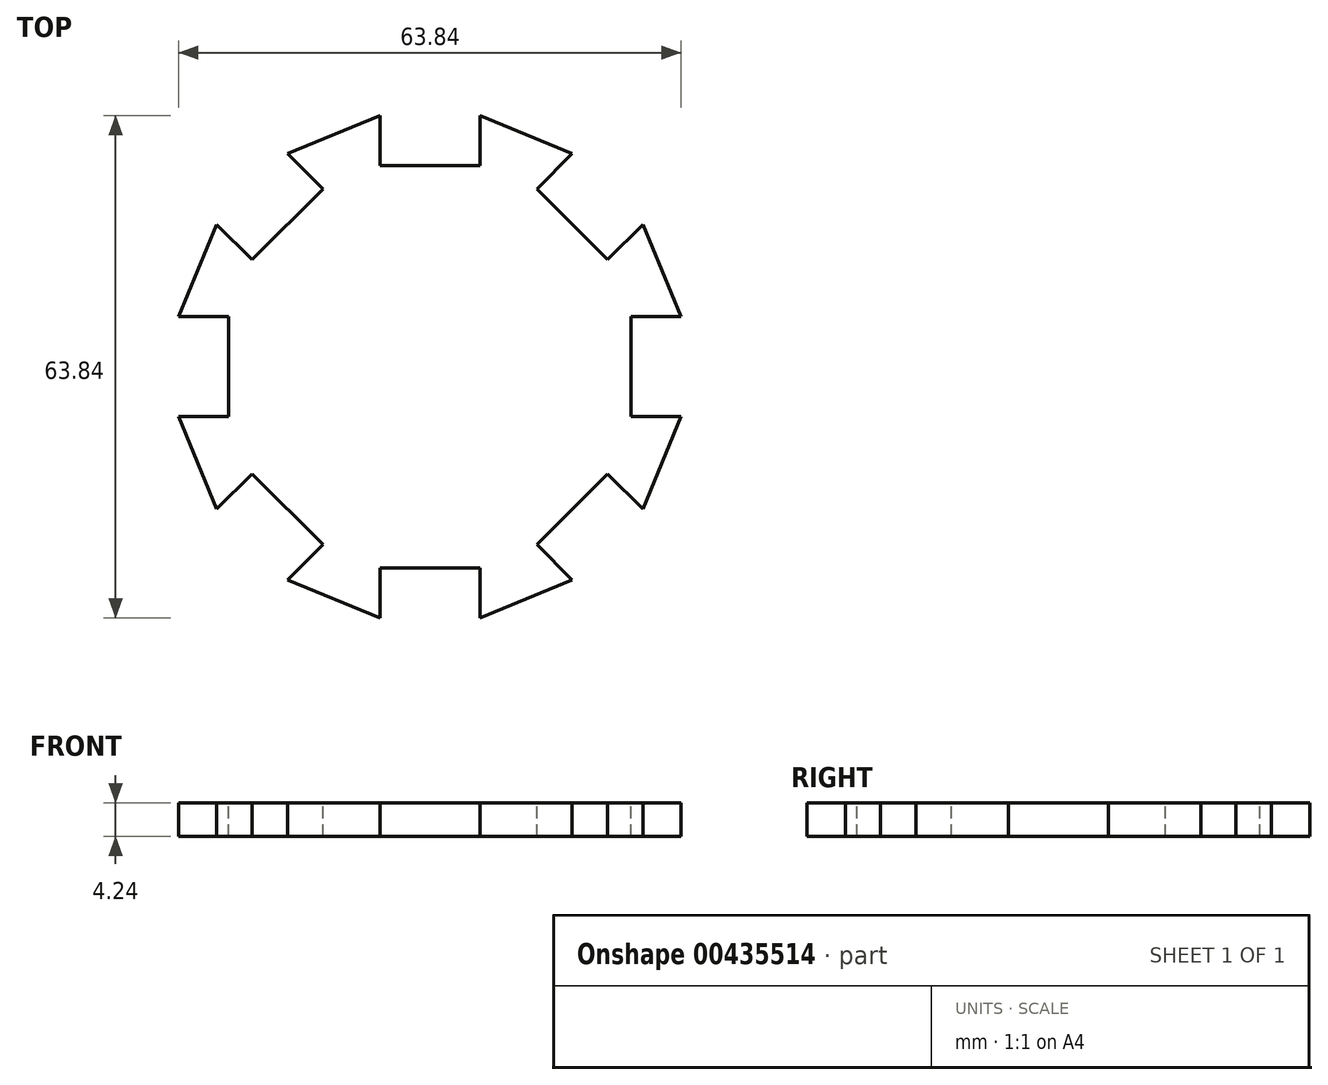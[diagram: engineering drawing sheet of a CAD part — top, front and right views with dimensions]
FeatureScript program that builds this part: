
annotation { "Feature Type Name" : "Feature", "Feature Type Description" : "" }
export const myFeature = defineFeature(function(context is Context, id is Id, definition is map)
    precondition{}
    {
        {
            var Q0;
            Q0=qCreatedBy(makeId("Top.planeOp"),FACE);
            var sketch = newSketch(context, id + "F0", { "sketchPlane" : qUnion([Q0])});
            skPoint(sketch, "E0.rect.middle", {"position": v(0, 0) * mm});
            skLineSegment(sketch, "E1.rect.bottom", {"start": v(-25.57, 6.35) * mm, "end": v(-38.27, 6.35) * mm});
            skLineSegment(sketch, "E1.rect.top", {"start": v(-25.57, -6.35) * mm, "end": v(-38.27, -6.35) * mm});
            skLineSegment(sketch, "E1.rect.left", {"start": v(-25.57, 6.35) * mm, "end": v(-25.57, -6.35) * mm});
            skLineSegment(sketch, "E1.rect.right", {"start": v(-38.27, 6.35) * mm, "end": v(-38.27, -6.35) * mm});
            skPoint(sketch, "E1.rect.middle", {"position": v(-31.92, 0) * mm});
            skLineSegment(sketch, "E2.rect.bottom", {"start": v(-6.35, 38.27) * mm, "end": v(6.35, 38.27) * mm});
            skLineSegment(sketch, "E2.rect.top", {"start": v(-6.35, 25.57) * mm, "end": v(6.35, 25.57) * mm});
            skLineSegment(sketch, "E2.rect.left", {"start": v(-6.35, 38.27) * mm, "end": v(-6.35, 25.57) * mm});
            skLineSegment(sketch, "E2.rect.right", {"start": v(6.35, 38.27) * mm, "end": v(6.35, 25.57) * mm});
            skPoint(sketch, "E2.rect.middle", {"position": v(0, 31.92) * mm});
            skLineSegment(sketch, "E3.rect.bottom", {"start": v(38.27, -6.35) * mm, "end": v(25.57, -6.35) * mm});
            skLineSegment(sketch, "E3.rect.top", {"start": v(38.27, 6.35) * mm, "end": v(25.57, 6.35) * mm});
            skLineSegment(sketch, "E3.rect.left", {"start": v(38.27, -6.35) * mm, "end": v(38.27, 6.35) * mm});
            skLineSegment(sketch, "E3.rect.right", {"start": v(25.57, -6.35) * mm, "end": v(25.57, 6.35) * mm});
            skPoint(sketch, "E3.rect.middle", {"position": v(31.92, 0) * mm});
            skLineSegment(sketch, "E4.rect.bottom", {"start": v(-6.35, -38.27) * mm, "end": v(6.35, -38.27) * mm});
            skLineSegment(sketch, "E4.rect.top", {"start": v(-6.35, -25.57) * mm, "end": v(6.35, -25.57) * mm});
            skLineSegment(sketch, "E4.rect.left", {"start": v(-6.35, -38.27) * mm, "end": v(-6.35, -25.57) * mm});
            skLineSegment(sketch, "E4.rect.right", {"start": v(6.35, -38.27) * mm, "end": v(6.35, -25.57) * mm});
            skPoint(sketch, "E4.rect.middle", {"position": v(0, -31.92) * mm});
            skLineSegment(sketch, "E5", {"start": v(-31.92, 6.35) * mm, "end": v(-27.06, 18.08) * mm});
            skLineSegment(sketch, "E6", {"start": v(-27.06, 18.08) * mm, "end": v(-18.08, 27.06) * mm});
            skLineSegment(sketch, "E7", {"start": v(-18.08, 27.06) * mm, "end": v(-6.35, 31.92) * mm});
            skLineSegment(sketch, "E8", {"start": v(6.35, 31.92) * mm, "end": v(18.08, 27.06) * mm});
            skLineSegment(sketch, "E9", {"start": v(18.08, 27.06) * mm, "end": v(27.06, 18.08) * mm});
            skLineSegment(sketch, "E10", {"start": v(27.06, 18.08) * mm, "end": v(31.92, 6.35) * mm});
            skLineSegment(sketch, "E11", {"start": v(31.92, -6.35) * mm, "end": v(27.06, -18.08) * mm});
            skLineSegment(sketch, "E12", {"start": v(27.06, -18.08) * mm, "end": v(18.08, -27.06) * mm});
            skLineSegment(sketch, "E13", {"start": v(18.08, -27.06) * mm, "end": v(6.35, -31.92) * mm});
            skLineSegment(sketch, "E14", {"start": v(-6.35, -31.92) * mm, "end": v(-18.08, -27.06) * mm});
            skLineSegment(sketch, "E15", {"start": v(-18.08, -27.06) * mm, "end": v(-27.06, -18.08) * mm});
            skLineSegment(sketch, "E16", {"start": v(-27.06, -18.08) * mm, "end": v(-31.92, -6.35) * mm});
            skLineSegment(sketch, "E17", {"start": v(-6.35, -31.92) * mm, "end": v(6.35, -31.92) * mm});
            skLineSegment(sketch, "E18", {"start": v(-31.92, 6.35) * mm, "end": v(-31.92, -6.35) * mm});
            skLineSegment(sketch, "E19", {"start": v(-6.35, 31.92) * mm, "end": v(6.35, 31.92) * mm});
            skLineSegment(sketch, "E20", {"start": v(31.92, 6.35) * mm, "end": v(31.92, -6.35) * mm});
            skLineSegment(sketch, "E21", {"start": v(13.6, 22.57) * mm, "end": v(22.57, 31.55) * mm});
            skLineSegment(sketch, "E22", {"start": v(22.57, 31.55) * mm, "end": v(31.55, 22.57) * mm});
            skLineSegment(sketch, "E23", {"start": v(31.55, 22.57) * mm, "end": v(22.57, 13.6) * mm});
            skLineSegment(sketch, "E24", {"start": v(22.57, 13.6) * mm, "end": v(13.6, 22.57) * mm});
            skLineSegment(sketch, "E25", {"start": v(-22.57, 31.55) * mm, "end": v(-13.6, 22.57) * mm});
            skLineSegment(sketch, "E26", {"start": v(-31.55, 22.57) * mm, "end": v(-22.57, 31.55) * mm});
            skLineSegment(sketch, "E27", {"start": v(-22.57, 13.6) * mm, "end": v(-31.55, 22.57) * mm});
            skLineSegment(sketch, "E28", {"start": v(-13.6, 22.57) * mm, "end": v(-22.57, 13.6) * mm});
            skLineSegment(sketch, "E29", {"start": v(-22.57, -13.6) * mm, "end": v(-13.6, -22.57) * mm});
            skLineSegment(sketch, "E30", {"start": v(-31.55, -22.57) * mm, "end": v(-22.57, -13.6) * mm});
            skLineSegment(sketch, "E31", {"start": v(-22.57, -31.55) * mm, "end": v(-31.55, -22.57) * mm});
            skLineSegment(sketch, "E32", {"start": v(-13.6, -22.57) * mm, "end": v(-22.57, -31.55) * mm});
            skLineSegment(sketch, "E33", {"start": v(22.57, -13.6) * mm, "end": v(31.55, -22.57) * mm});
            skLineSegment(sketch, "E34", {"start": v(13.6, -22.57) * mm, "end": v(22.57, -13.6) * mm});
            skLineSegment(sketch, "E35", {"start": v(22.57, -31.55) * mm, "end": v(13.6, -22.57) * mm});
            skLineSegment(sketch, "E36", {"start": v(31.55, -22.57) * mm, "end": v(22.57, -31.55) * mm});
            skSolve(sketch);
        }
        {
            var Q0;
            {var subQ13=sQuery(id+"F0.wireOp",EDGE,"E1.rect.left");Q0=makeQuery(id+"F0.imprint","IMPRINT",FACE,{"disambiguationData":[TD([[makeQuery(id+"F0.imprint","IMPRINT",EDGE,{"derivedFrom":subQ13}),1.0]])]});}
            extrude(context, id + "F1", {"entities" : qUnion([Q0]), "oppositeDirection" : true, "depth" : 2.12 * mm, "hasSecondDirection" : true, "secondDirectionOppositeDirection" : false, "secondDirectionDepth" : 2.12 * mm});
        }
    });
